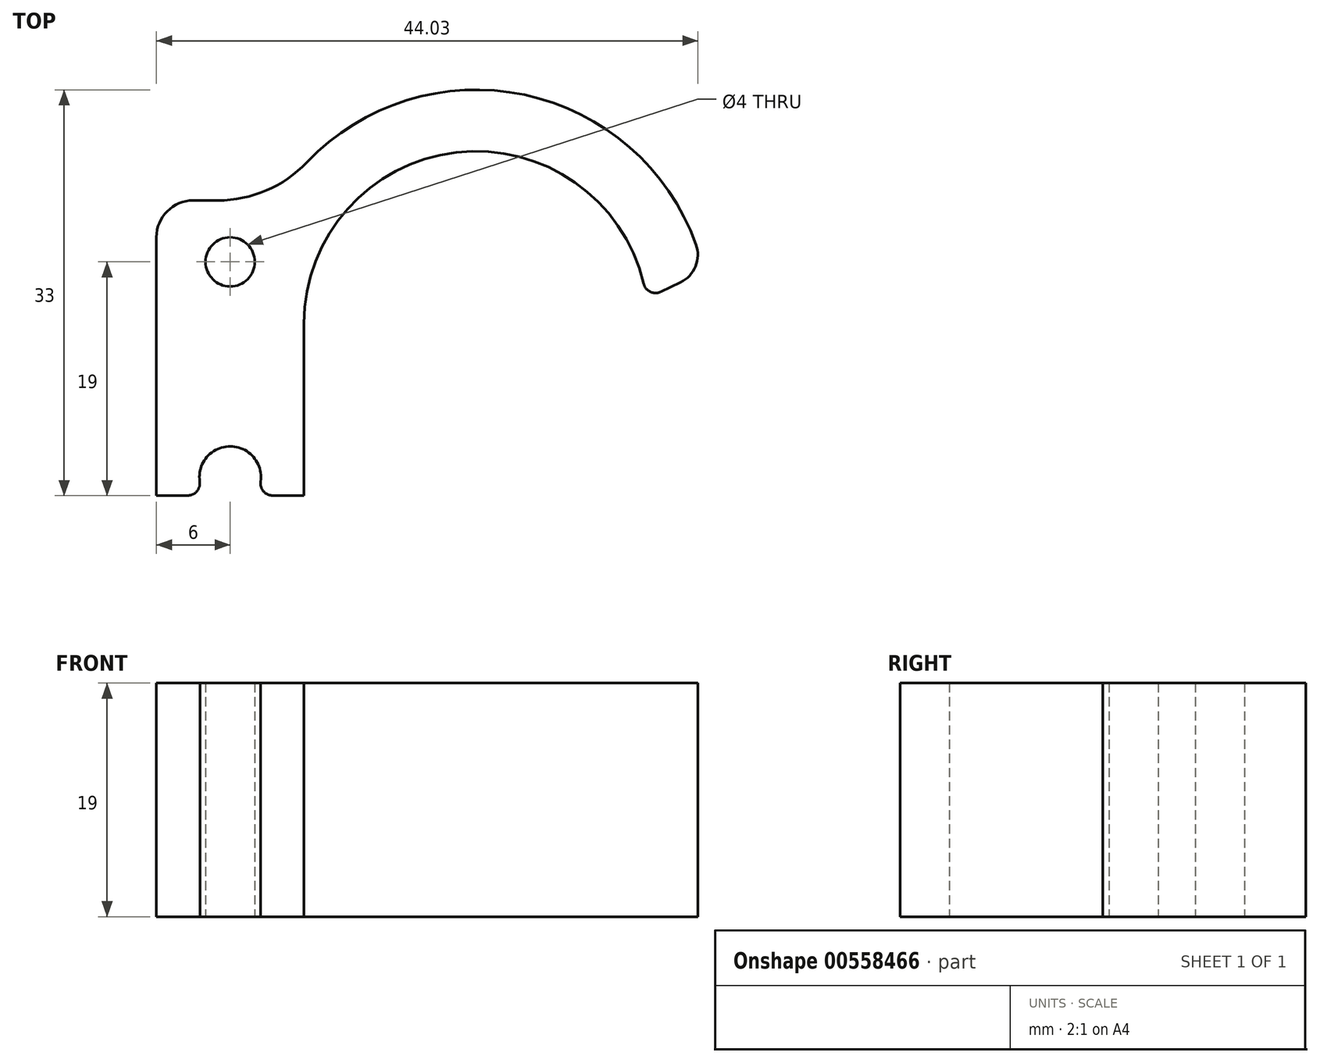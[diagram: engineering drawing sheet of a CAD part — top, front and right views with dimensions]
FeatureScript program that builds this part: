
annotation { "Feature Type Name" : "Feature", "Feature Type Description" : "" }
export const myFeature = defineFeature(function(context is Context, id is Id, definition is map)
    precondition{}
    {
        {
            var Q0;
            Q0=qCreatedBy(makeId("Top.planeOp"),FACE);
            var sketch = newSketch(context, id + "F0", { "sketchPlane" : qUnion([Q0])});
            skLineSegment(sketch, "E0.bottom", {"start": v(0, 0) * mm, "end": v(12, 0) * mm});
            skLineSegment(sketch, "E0.top", {"start": v(0, 24) * mm, "end": v(12, 24) * mm});
            skLineSegment(sketch, "E0.left", {"start": v(0, 0) * mm, "end": v(0, 24) * mm});
            skLineSegment(sketch, "E0.right", {"start": v(12, 0) * mm, "end": v(12, 24) * mm});
            skPoint(sketch, "E1", {"position": v(26, 14) * mm});
            skArc(sketch, "E2", {"start": v(39.86, 16) * mm, "mid": v(25, 27.96) * mm, "end": v(12, 14) * mm});
            skArc(sketch, "E3", {"start": v(44.52, 18.25) * mm, "mid": v(29.1, 32.74) * mm, "end": v(9.84, 24) * mm});
            skLineSegment(sketch, "E4", {"start": v(44.52, 18.25) * mm, "end": v(39.86, 16) * mm});
            skCircle(sketch, "E5", {"center": v(6, 19) * mm, "radius": 2 * mm});
            skCircle(sketch, "E6", {"center": v(6, 1.5) * mm, "radius": 2.5 * mm});
            skSolve(sketch);
        }
        {
            var Q0;
            {var subQ4=sQuery(id+"F0.wireOp",EDGE,"E0.left");Q0=makeQuery(id+"F0.imprint","IMPRINT",FACE,{"disambiguationData":[TD([[makeQuery(id+"F0.imprint","IMPRINT",EDGE,{"derivedFrom":subQ4}),-1.0]])]});}
            var Q1;
            {var subQ0=sQuery(id+"F0.wireOp",EDGE,"E2");Q1=makeQuery(id+"F0.imprint","IMPRINT",FACE,{"disambiguationData":[TD([[makeQuery(id+"F0.imprint","IMPRINT",EDGE,{"derivedFrom":subQ0}),-1.0]])]});}
            extrude(context, id + "F1", {"entities" : qUnion([Q0, Q1]), "depth" : 19 * mm, "offsetDistance" : 25 * mm});
        }
        {
            var Q0;
            Q0=makeQuery(id+"F1.opExtrude","SWEPT_EDGE",EDGE,{"disambiguationData":[OSD([sQuery(id+"F0.wireOp",EDGE,"E0.top"),sQuery(id+"F0.wireOp",EDGE,"E0.left")])]});
            fillet(context, id + "F2", {"entities" : qUnion([Q0]), "radius" : 3 * mm, "tangentPropagation" : true, "allowEdgeOverflow" : false});
        }
        {
            var Q0;
            Q0=makeQuery(id+"F1.opExtrude","SWEPT_EDGE",EDGE,{"disambiguationData":[OSD([sQuery(id+"F0.wireOp",EDGE,"E0.top"),sQuery(id+"F0.wireOp",EDGE,"E3")])]});
            fillet(context, id + "F3", {"entities" : qUnion([Q0]), "radius" : 10 * mm, "tangentPropagation" : true, "allowEdgeOverflow" : false});
        }
        {
            var Q0;
            Q0=makeQuery(id+"F1.opExtrude","SWEPT_EDGE",EDGE,{"disambiguationData":[OSD([sQuery(id+"F0.wireOp",EDGE,"E3"),sQuery(id+"F0.wireOp",EDGE,"E4")])]});
            fillet(context, id + "F4", {"entities" : qUnion([Q0]), "radius" : 2.5 * mm, "tangentPropagation" : true, "allowEdgeOverflow" : false});
        }
        {
            var Q0;
            Q0=makeQuery(id+"F1.opExtrude","SWEPT_EDGE",EDGE,{"disambiguationData":[OSD([sQuery(id+"F0.wireOp",EDGE,"E2"),sQuery(id+"F0.wireOp",EDGE,"E4")])]});
            fillet(context, id + "F5", {"entities" : qUnion([Q0]), "radius" : 1 * mm, "tangentPropagation" : true, "allowEdgeOverflow" : false});
        }
        {
            var Q0;
            {var subQ0=sQuery(id+"F0.wireOp",EDGE,"E6");var subQ1=sQuery(id+"F0.wireOp",EDGE,"E0.bottom");Q0=makeQuery(id+"F1.opExtrude","SWEPT_EDGE",EDGE,{"disambiguationData":[OSD([subQ1,subQ0]),TDD([makeQuery(id+"F0.imprint","INTERSECT",VERTEX,{"disambiguationData":[OD(0.0)],"derivedFrom":[subQ1,subQ0]})])]});}
            var Q1;
            {var subQ0=sQuery(id+"F0.wireOp",EDGE,"E6");var subQ1=sQuery(id+"F0.wireOp",EDGE,"E0.bottom");Q1=makeQuery(id+"F1.opExtrude","SWEPT_EDGE",EDGE,{"disambiguationData":[OSD([subQ1,subQ0]),TDD([makeQuery(id+"F0.imprint","INTERSECT",VERTEX,{"disambiguationData":[OD(1.0)],"derivedFrom":[subQ1,subQ0]})])]});}
            fillet(context, id + "F6", {"entities" : qUnion([Q0, Q1]), "radius" : 1 * mm, "tangentPropagation" : true, "allowEdgeOverflow" : false});
        }
    });
